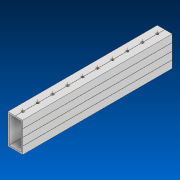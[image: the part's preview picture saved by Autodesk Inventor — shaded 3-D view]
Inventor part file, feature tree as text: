
AUTODESK INVENTOR PART (.ipt)
format: ipt  version: 2022.2 (Build 262287000, 287)  size: 445,952 bytes
history: native  units: in
note: dims shown in document units (in); Inventor stores cm internally (conversion verified against a paired STEP export)
features: other x11, extrude x1, pattern_linear x1, sketch x1
ambient origin geometry x8: Origin, YZ Plane, XZ Plane, XY Plane, X Axis, Y Axis, Z Axis, Center Point
bodies: Solid1 (feature_tree)
feature tree (14):
  extrude  "Extrusion1"  Depth=2.0in
  other  "Work Axis1"
  pattern_linear  "Rectangular Pattern1"  Spacing1=49.0in  [1 undecoded]
  sketch  "Sketch1"  dims[d0=1.0in d1=2.0in d2=49.0in d3=0.0in d4=3.937in d6=1.0in]
  other  "Work Axis2"
  other  "Work Axis3"
  other  "Work Axis4"
  other  "Work Axis5"
  other  "Work Axis6"
  other  "Work Axis7"
  other  "Work Axis8"
  other  "Work Axis9"
  other  "Work Axis10"
  other  "Cut-Extrude2"
note: 1 required parameter value undecoded (feature->parameter linkage not recoverable at this tier; creation-order binding heuristic only, values carry confidence <= 0.55)
